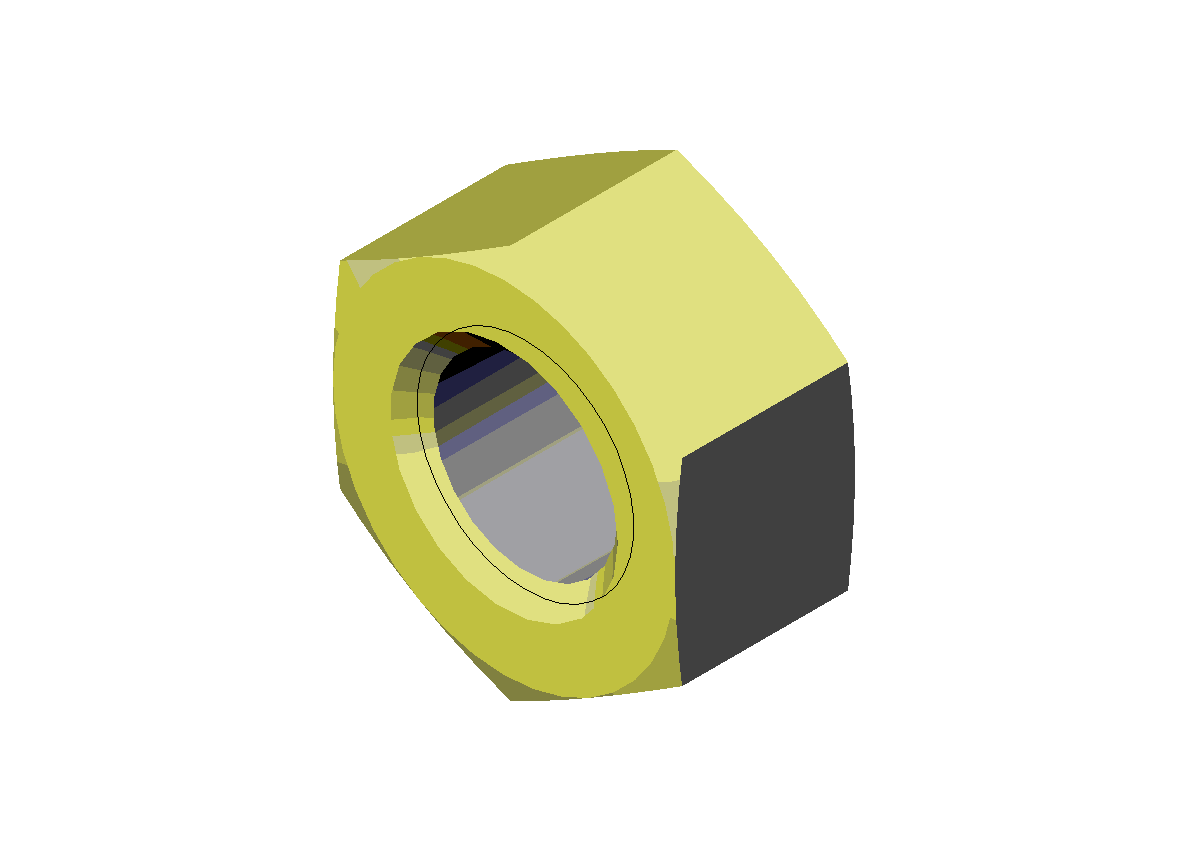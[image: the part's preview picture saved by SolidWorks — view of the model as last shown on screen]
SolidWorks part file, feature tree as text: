
SOLIDWORKS PART (.sldprt)
format: sldprt  version: not decoded by parser v0  size: 168,960 bytes
history: native  units: mm
features: plane x3, sketch x3, extrude x1, cut_revolve x1, thread x1, chamfer x1 (+8 scaffold rows collapsed)
feature tree (18):
  scaffold x8  (default folders/planes/origin — collapsed)
  plane  "Ebene1"
  plane  "Ebene2"
  plane  "Ebene3"
  sketch  "Skizze1"  dims[c1.SW=19.0mm c1.D2=~5.198289mm c2.D2=120.0deg]
  extrude  "Basis-Linear austragen"  Depth=10mm
  sketch  "Skizze2"  dims[c1.D1=9.5mm c1.D2=~6.762286mm c2.D2=15.0deg c2.D3=2.0mm c2.D4=0.5mm]
  cut_revolve  "Schnitt-Rotation1"  Angle=360deg
  sketch  "Skizze3"  dims[D1=10.25mm]
  thread  "Gewindedarstellung1"  [2 undecoded]
  chamfer  "Fase1"  Distance=1.2mm Angle=45deg
decode coverage: 6 of 7 modeling features carry decoded parameters
note: ~ marks probable driven/reference dimensions
note: 2 parameter values undecoded
note: suppression state not decoded; provenance and decode notes live in map.json
